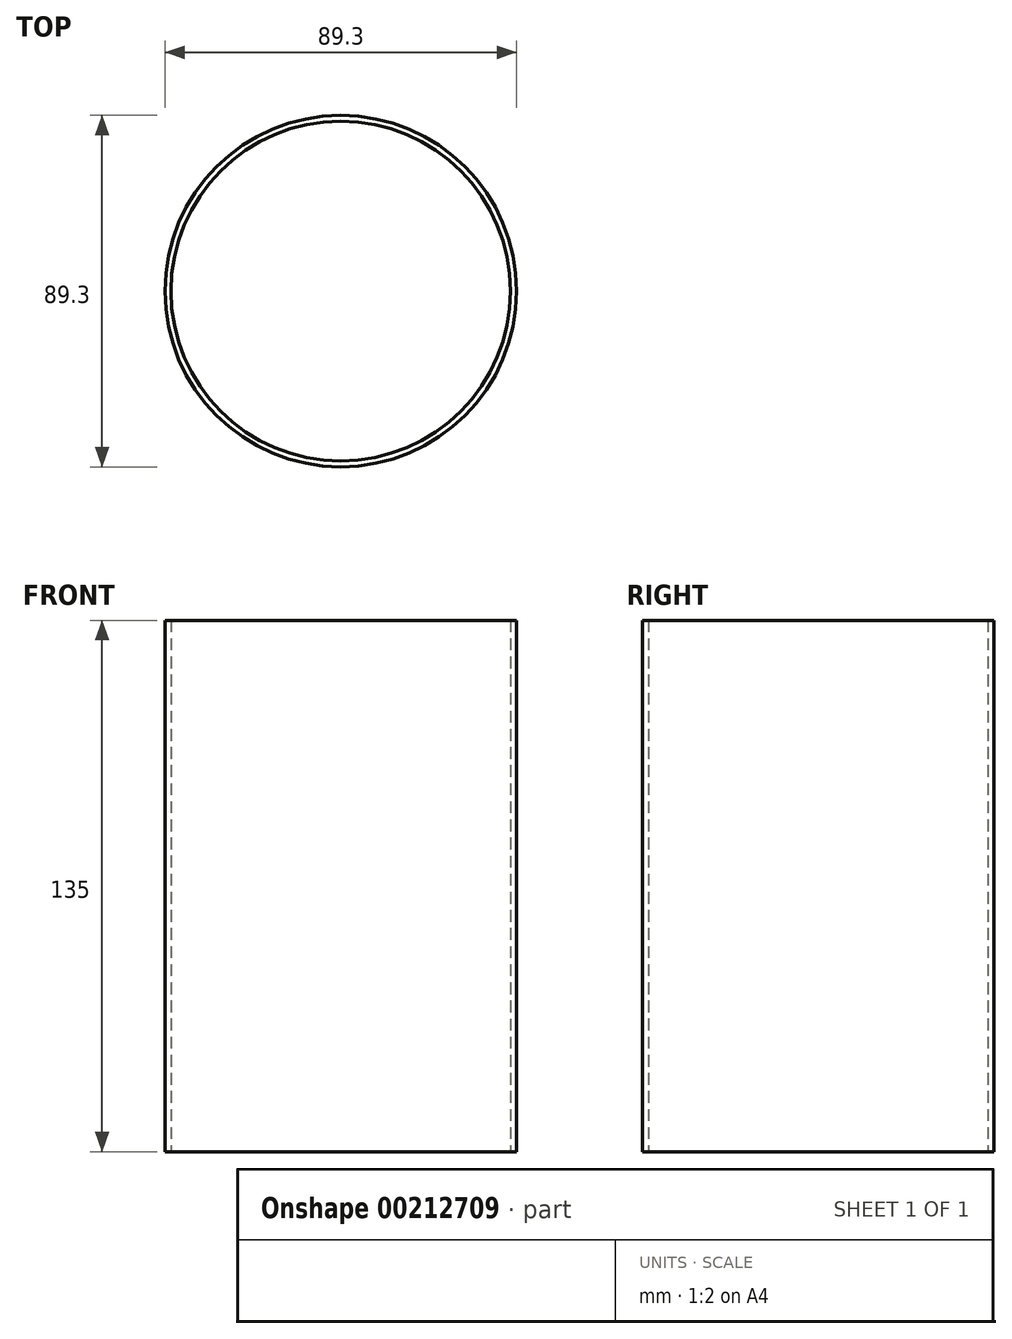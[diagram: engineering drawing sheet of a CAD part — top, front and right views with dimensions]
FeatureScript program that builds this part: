
annotation { "Feature Type Name" : "Feature", "Feature Type Description" : "" }
export const myFeature = defineFeature(function(context is Context, id is Id, definition is map)
    precondition{}
    {
        {
            var Q0;
            Q0=qCreatedBy(makeId("Top.planeOp"),FACE);
            var sketch = newSketch(context, id + "F0", { "sketchPlane" : qUnion([Q0])});
            skCircle(sketch, "E0", {"center": v(31.22, 31.58) * mm, "radius": 44.65 * mm});
            skCircle(sketch, "E1", {"center": v(31.22, 31.58) * mm, "radius": 43.15 * mm});
            skSolve(sketch);
        }
        {
            var Q0;
            Q0 = qSketchRegion(id + "F0", true);
            extrude(context, id + "F1", {"entities" : qUnion([Q0]), "depth" : 135 * mm});
        }
    });
